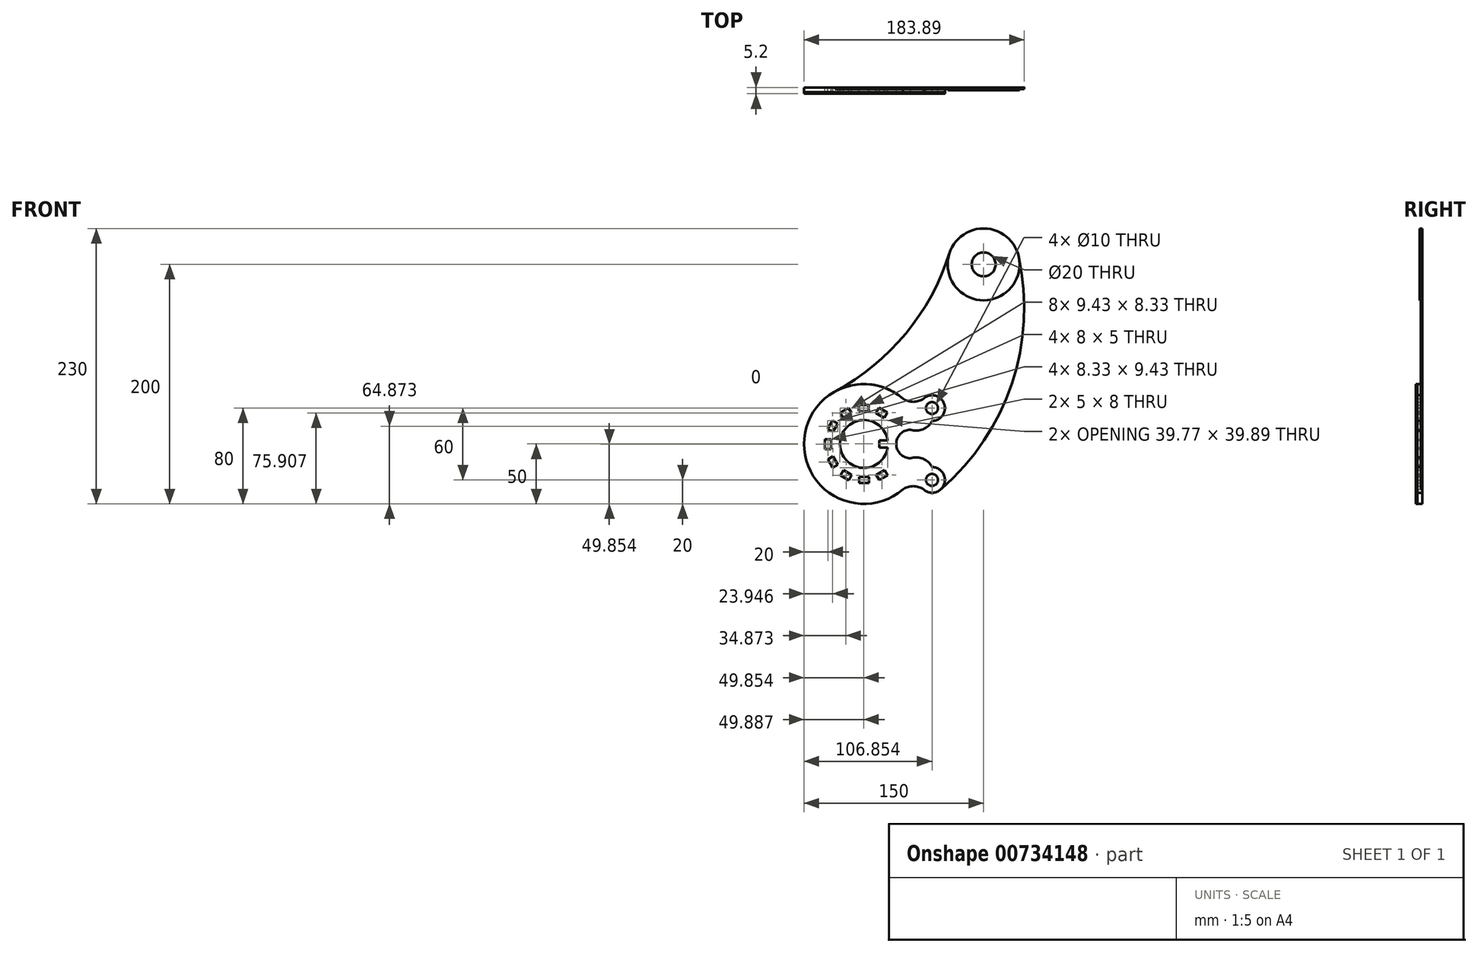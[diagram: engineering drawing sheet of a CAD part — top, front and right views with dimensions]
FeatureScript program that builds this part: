
annotation { "Feature Type Name" : "Feature", "Feature Type Description" : "" }
export const myFeature = defineFeature(function(context is Context, id is Id, definition is map)
    precondition{}
    {
        {
            var Q0;
            Q0=qCreatedBy(makeId("Front.planeOp"),FACE);
            var sketch = newSketch(context, id + "F0", { "sketchPlane" : qUnion([Q0])});
            skLineSegment(sketch, "E0", {"start": v(-37.23, -27) * mm, "end": v(-44.23, -27) * mm});
            skLineSegment(sketch, "E1", {"start": v(-37.23, -33) * mm, "end": v(-44.23, -33) * mm});
            skLineSegment(sketch, "E2", {"start": v(-44.23, -27) * mm, "end": v(-44.23, -33) * mm});
            skArc(sketch, "E3", {"start": v(-37.23, -27) * mm, "mid": v(-77, -30) * mm, "end": v(-37.23, -33) * mm});
            skArc(sketch, "E4", {"start": v(-24.54, 8.03) * mm, "mid": v(-107, -30) * mm, "end": v(-24.54, -68.03) * mm});
            skLineSegment(sketch, "E5.bottom", {"start": v(-61.15, 2.5) * mm, "end": v(-53.15, 2.5) * mm});
            skLineSegment(sketch, "E5.top", {"start": v(-61.15, -2.5) * mm, "end": v(-53.15, -2.5) * mm});
            skLineSegment(sketch, "E5.left", {"start": v(-61.15, 2.5) * mm, "end": v(-61.15, -2.5) * mm});
            skLineSegment(sketch, "E5.right", {"start": v(-53.15, 2.5) * mm, "end": v(-53.15, -2.5) * mm});
            skPoint(sketch, "E5.middle", {"position": v(-57.15, 0) * mm});
            skPoint(sketch, "E6.middle", {"position": v(-61.15, 2.5) * mm});
            skLineSegment(sketch, "E7.1.0", {"start": v(-76.84, -3.93) * mm, "end": v(-74.34, -8.26) * mm});
            skLineSegment(sketch, "E7.1.1", {"start": v(-74.34, -8.26) * mm, "end": v(-67.41, -4.26) * mm});
            skLineSegment(sketch, "E7.1.2", {"start": v(-69.91, 0.07) * mm, "end": v(-67.41, -4.26) * mm});
            skLineSegment(sketch, "E7.1.3", {"start": v(-76.84, -3.93) * mm, "end": v(-69.91, 0.07) * mm});
            skLineSegment(sketch, "E7.2.0", {"start": v(-87.22, -17.34) * mm, "end": v(-82.89, -19.84) * mm});
            skLineSegment(sketch, "E7.2.1", {"start": v(-82.89, -19.84) * mm, "end": v(-78.89, -12.91) * mm});
            skLineSegment(sketch, "E7.2.2", {"start": v(-83.22, -10.41) * mm, "end": v(-78.89, -12.91) * mm});
            skLineSegment(sketch, "E7.2.3", {"start": v(-87.22, -17.34) * mm, "end": v(-83.22, -10.41) * mm});
            skLineSegment(sketch, "E7.3.0", {"start": v(-89.5, -34.15) * mm, "end": v(-84.5, -34.15) * mm});
            skLineSegment(sketch, "E7.3.1", {"start": v(-84.5, -34.15) * mm, "end": v(-84.5, -26.15) * mm});
            skLineSegment(sketch, "E7.3.2", {"start": v(-89.5, -26.15) * mm, "end": v(-84.5, -26.15) * mm});
            skLineSegment(sketch, "E7.3.3", {"start": v(-89.5, -34.15) * mm, "end": v(-89.5, -26.15) * mm});
            skLineSegment(sketch, "E7.4.0", {"start": v(-83.07, -49.84) * mm, "end": v(-78.74, -47.34) * mm});
            skLineSegment(sketch, "E7.4.1", {"start": v(-78.74, -47.34) * mm, "end": v(-82.74, -40.41) * mm});
            skLineSegment(sketch, "E7.4.2", {"start": v(-87.07, -42.91) * mm, "end": v(-82.74, -40.41) * mm});
            skLineSegment(sketch, "E7.4.3", {"start": v(-83.07, -49.84) * mm, "end": v(-87.07, -42.91) * mm});
            skLineSegment(sketch, "E7.5.0", {"start": v(-69.66, -60.22) * mm, "end": v(-67.16, -55.89) * mm});
            skLineSegment(sketch, "E7.5.1", {"start": v(-67.16, -55.89) * mm, "end": v(-74.09, -51.89) * mm});
            skLineSegment(sketch, "E7.5.2", {"start": v(-76.59, -56.22) * mm, "end": v(-74.09, -51.89) * mm});
            skLineSegment(sketch, "E7.5.3", {"start": v(-69.66, -60.22) * mm, "end": v(-76.59, -56.22) * mm});
            skLineSegment(sketch, "E7.6.0", {"start": v(-52.85, -62.5) * mm, "end": v(-52.85, -57.5) * mm});
            skLineSegment(sketch, "E7.6.1", {"start": v(-52.85, -57.5) * mm, "end": v(-60.85, -57.5) * mm});
            skLineSegment(sketch, "E7.6.2", {"start": v(-60.85, -62.5) * mm, "end": v(-60.85, -57.5) * mm});
            skLineSegment(sketch, "E7.6.3", {"start": v(-52.85, -62.5) * mm, "end": v(-60.85, -62.5) * mm});
            skLineSegment(sketch, "E7.7.0", {"start": v(-37.16, -56.07) * mm, "end": v(-39.66, -51.74) * mm});
            skLineSegment(sketch, "E7.7.1", {"start": v(-39.66, -51.74) * mm, "end": v(-46.59, -55.74) * mm});
            skLineSegment(sketch, "E7.7.2", {"start": v(-44.09, -60.07) * mm, "end": v(-46.59, -55.74) * mm});
            skLineSegment(sketch, "E7.7.3", {"start": v(-37.16, -56.07) * mm, "end": v(-44.09, -60.07) * mm});
            skLineSegment(sketch, "E7.11.0", {"start": v(-44.34, 0.22) * mm, "end": v(-46.84, -4.11) * mm});
            skLineSegment(sketch, "E7.11.1", {"start": v(-46.84, -4.11) * mm, "end": v(-39.91, -8.11) * mm});
            skLineSegment(sketch, "E7.11.2", {"start": v(-37.41, -3.78) * mm, "end": v(-39.91, -8.11) * mm});
            skLineSegment(sketch, "E7.11.3", {"start": v(-44.34, 0.22) * mm, "end": v(-37.41, -3.78) * mm});
            skCircle(sketch, "E8", {"center": v(43, 120) * mm, "radius": 10 * mm});
            skCircle(sketch, "E9", {"center": v(43, 120) * mm, "radius": 30 * mm});
            skArc(sketch, "E10", {"start": v(-80.83, 13.95) * mm, "mid": v(-22.05, 62.3) * mm, "end": v(14.41, 129.1) * mm});
            skLineSegment(sketch, "E11", {"start": v(-57, -30) * mm, "end": v(74.12, -30) * mm, "construction": true});
            skCircle(sketch, "E12", {"center": v(-0.15, 0) * mm, "radius": 5 * mm});
            skCircle(sketch, "E13.MirrorC", {"center": v(-0.15, -60) * mm, "radius": 5 * mm});
            skArc(sketch, "E14", {"start": v(10.7, 0) * mm, "mid": v(7.56, 7.56) * mm, "end": v(0, 10.7) * mm});
            skArc(sketch, "E15.MirrorCS", {"start": v(10.7, -60) * mm, "mid": v(7.56, -67.56) * mm, "end": v(0, -70.7) * mm});
            skArc(sketch, "E16.MirrorCS", {"start": v(10.7, 0) * mm, "mid": v(7.56, -7.56) * mm, "end": v(0, -10.7) * mm});
            skArc(sketch, "E17.MirrorCS", {"start": v(10.7, -60) * mm, "mid": v(7.56, -52.44) * mm, "end": v(0, -49.3) * mm});
            skArc(sketch, "E18", {"start": v(0, 10.7) * mm, "mid": v(-3.77, 10) * mm, "end": v(-7.06, 8.03) * mm});
            skArc(sketch, "E19.MirrorCS", {"start": v(0, -70.7) * mm, "mid": v(-3.77, -70) * mm, "end": v(-7.06, -68.03) * mm});
            skArc(sketch, "E20", {"start": v(-24.54, 8.03) * mm, "mid": v(-15.8, 5.22) * mm, "end": v(-7.06, 8.03) * mm});
            skArc(sketch, "E21.MirrorCS", {"start": v(-24.54, -68.03) * mm, "mid": v(-15.8, -65.22) * mm, "end": v(-7.06, -68.03) * mm});
            skPoint(sketch, "E22.orphan", {"position": v(-8.46, -18) * mm});
            skPoint(sketch, "E23.orphan", {"position": v(-8.46, -42) * mm});
            skArc(sketch, "E24", {"start": v(7.56, -67.56) * mm, "mid": v(66.6, 20.5) * mm, "end": v(72.31, 126.38) * mm});
            skArc(sketch, "E25", {"start": v(-18.2, -18) * mm, "mid": v(-7.74, -17.73) * mm, "end": v(0, -10.7) * mm});
            skArc(sketch, "E26.MirrorCS", {"start": v(-18.2, -42) * mm, "mid": v(-7.74, -42.27) * mm, "end": v(0, -49.3) * mm});
            skArc(sketch, "E27", {"start": v(-18.2, -18) * mm, "mid": v(-29.99, -30) * mm, "end": v(-18.2, -42) * mm});
            skSolve(sketch);
        }
        {
            var Q0;
            Q0=makeQuery(id+"F0.imprint","IMPRINT",FACE,{"disambiguationData":[TD([[makeQuery(id+"F0.imprint","IMPRINT",EDGE,{"derivedFrom":sQuery(id+"F0.wireOp",EDGE,"E8")}),-1.0]])]});
            extrude(context, id + "F1", {"entities" : qUnion([Q0]), "depth" : 2.3 * mm, "offsetDistance" : 25 * mm});
        }
        {
            var Q0;
            Q0=makeQuery(id+"F0.imprint","IMPRINT",FACE,{"disambiguationData":[TD([[makeQuery(id+"F0.imprint","IMPRINT",EDGE,{"derivedFrom":sQuery(id+"F0.wireOp",EDGE,"E0")}),1.0]])]});
            extrude(context, id + "F2", {"entities" : qUnion([Q0]), "depth" : 4 * mm, "offsetDistance" : 25 * mm});
        }
        {
            var Q0;
            {var subQ5=sQuery(id+"F0.wireOp",EDGE,"E10");Q0=makeQuery(id+"F0.imprint","IMPRINT",FACE,{"disambiguationData":[TD([[makeQuery(id+"F0.imprint","IMPRINT",EDGE,{"derivedFrom":subQ5}),-1.0]])]});}
            var Q1;
            Q1=makeQuery(id+"F2.opExtrude","CAP_FACE",FACE,{"disambiguationData":[OSD([sQuery(id+"F0.wireOp",EDGE,"E0"),sQuery(id+"F0.wireOp",EDGE,"E1"),sQuery(id+"F0.wireOp",EDGE,"E2"),sQuery(id+"F0.wireOp",EDGE,"E3"),sQuery(id+"F0.wireOp",EDGE,"E4"),sQuery(id+"F0.wireOp",EDGE,"E5.bottom"),sQuery(id+"F0.wireOp",EDGE,"E5.top"),sQuery(id+"F0.wireOp",EDGE,"E5.left"),sQuery(id+"F0.wireOp",EDGE,"E5.right"),sQuery(id+"F0.wireOp",EDGE,"E7.1.0"),sQuery(id+"F0.wireOp",EDGE,"E7.1.1"),sQuery(id+"F0.wireOp",EDGE,"E7.1.2"),sQuery(id+"F0.wireOp",EDGE,"E7.1.3"),sQuery(id+"F0.wireOp",EDGE,"E7.2.0"),sQuery(id+"F0.wireOp",EDGE,"E7.2.1"),sQuery(id+"F0.wireOp",EDGE,"E7.2.2"),sQuery(id+"F0.wireOp",EDGE,"E7.2.3"),sQuery(id+"F0.wireOp",EDGE,"E7.3.0"),sQuery(id+"F0.wireOp",EDGE,"E7.3.1"),sQuery(id+"F0.wireOp",EDGE,"E7.3.2"),sQuery(id+"F0.wireOp",EDGE,"E7.3.3"),sQuery(id+"F0.wireOp",EDGE,"E7.4.0"),sQuery(id+"F0.wireOp",EDGE,"E7.4.1"),sQuery(id+"F0.wireOp",EDGE,"E7.4.2"),sQuery(id+"F0.wireOp",EDGE,"E7.4.3"),sQuery(id+"F0.wireOp",EDGE,"E7.5.0"),sQuery(id+"F0.wireOp",EDGE,"E7.5.1"),sQuery(id+"F0.wireOp",EDGE,"E7.5.2"),sQuery(id+"F0.wireOp",EDGE,"E7.5.3"),sQuery(id+"F0.wireOp",EDGE,"E7.6.0"),sQuery(id+"F0.wireOp",EDGE,"E7.6.1"),sQuery(id+"F0.wireOp",EDGE,"E7.6.2"),sQuery(id+"F0.wireOp",EDGE,"E7.6.3"),sQuery(id+"F0.wireOp",EDGE,"E7.7.0"),sQuery(id+"F0.wireOp",EDGE,"E7.7.1"),sQuery(id+"F0.wireOp",EDGE,"E7.7.2"),sQuery(id+"F0.wireOp",EDGE,"E7.7.3"),sQuery(id+"F0.wireOp",EDGE,"E7.11.0"),sQuery(id+"F0.wireOp",EDGE,"E7.11.1"),sQuery(id+"F0.wireOp",EDGE,"E7.11.2"),sQuery(id+"F0.wireOp",EDGE,"E7.11.3"),sQuery(id+"F0.wireOp",EDGE,"E12"),sQuery(id+"F0.wireOp",EDGE,"E13.MirrorC"),sQuery(id+"F0.wireOp",EDGE,"E14"),sQuery(id+"F0.wireOp",EDGE,"E16.MirrorCS"),sQuery(id+"F0.wireOp",EDGE,"E15.MirrorCS"),sQuery(id+"F0.wireOp",EDGE,"E17.MirrorCS"),sQuery(id+"F0.wireOp",EDGE,"E18"),sQuery(id+"F0.wireOp",EDGE,"E19.MirrorCS"),sQuery(id+"F0.wireOp",EDGE,"E20"),sQuery(id+"F0.wireOp",EDGE,"E21.MirrorCS"),sQuery(id+"F0.wireOp",EDGE,"E25"),sQuery(id+"F0.wireOp",EDGE,"E26.MirrorCS"),sQuery(id+"F0.wireOp",EDGE,"E27")])],"isStart":false});
            extrude(context, id + "F3", {"entities" : qUnion([Q0, Q1]), "depth" : 1.2 * mm, "offsetDistance" : 25 * mm});
        }
    });
